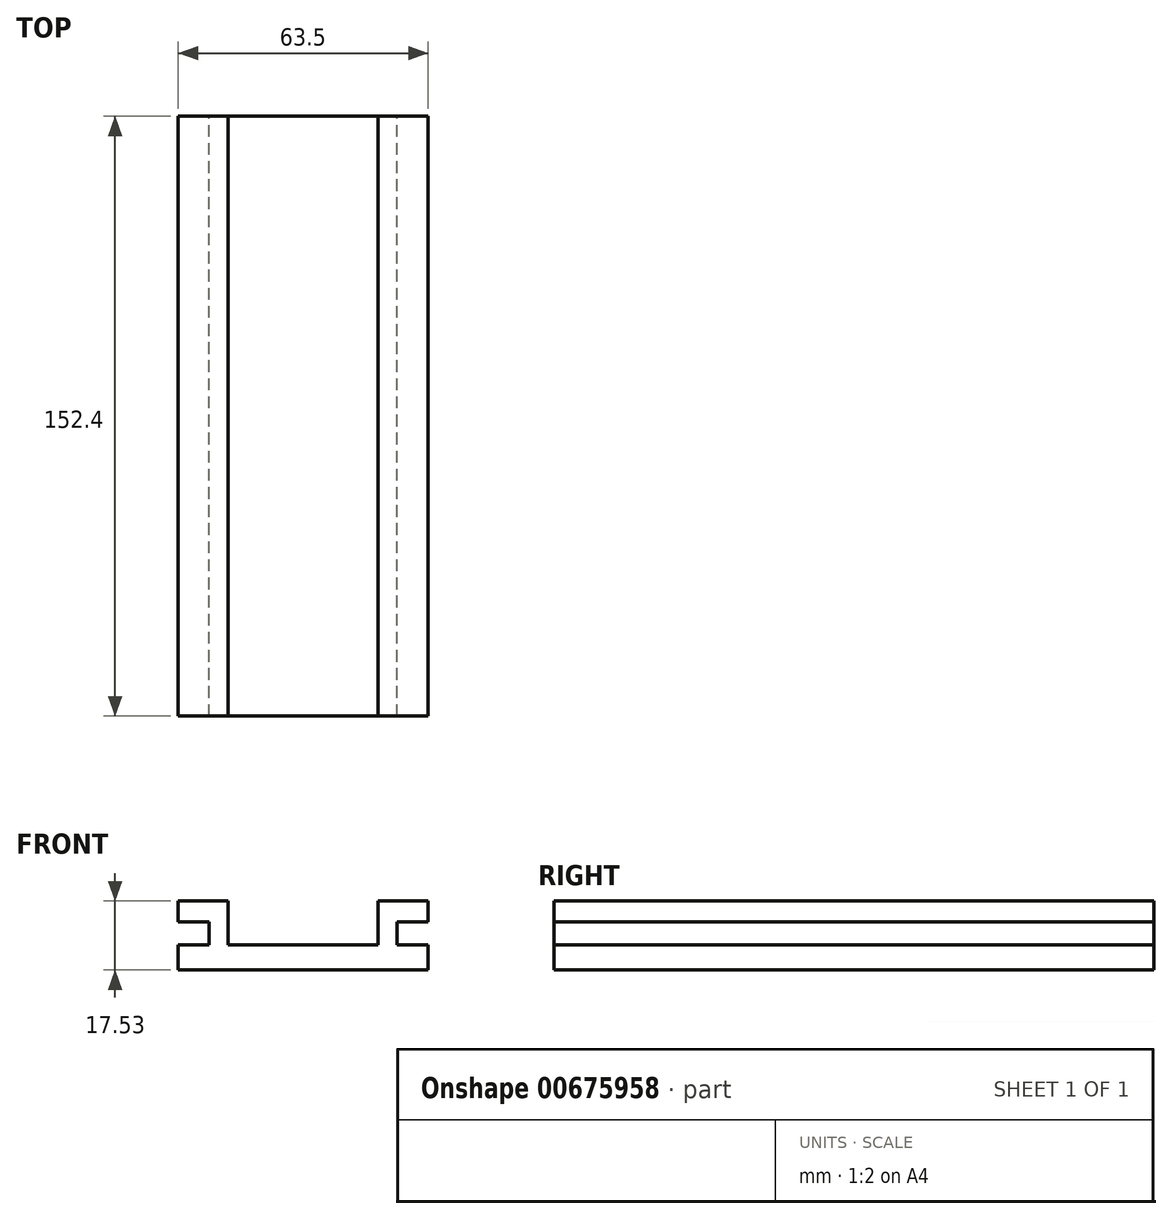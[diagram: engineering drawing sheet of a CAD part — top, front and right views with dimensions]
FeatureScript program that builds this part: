
annotation { "Feature Type Name" : "Feature", "Feature Type Description" : "" }
export const myFeature = defineFeature(function(context is Context, id is Id, definition is map)
    precondition{}
    {
        {
            var Q0;
            Q0=qCreatedBy(makeId("Front.planeOp"),FACE);
            var sketch = newSketch(context, id + "F0", { "sketchPlane" : qUnion([Q0])});
            skLineSegment(sketch, "E0", {"start": v(-31.75, 0) * mm, "end": v(-19.05, 0) * mm});
            skLineSegment(sketch, "E1", {"start": v(-31.75, 0) * mm, "end": v(-31.75, -5.33) * mm});
            skLineSegment(sketch, "E2", {"start": v(-31.75, -5.33) * mm, "end": v(-23.88, -5.33) * mm});
            skLineSegment(sketch, "E3", {"start": v(-23.88, -5.33) * mm, "end": v(-23.88, -11.18) * mm});
            skLineSegment(sketch, "E4", {"start": v(-23.88, -11.18) * mm, "end": v(-31.75, -11.18) * mm});
            skLineSegment(sketch, "E5", {"start": v(-31.75, -11.18) * mm, "end": v(-31.75, -17.53) * mm});
            skLineSegment(sketch, "E6", {"start": v(-19.05, 0) * mm, "end": v(-19.05, -11.18) * mm});
            skLineSegment(sketch, "E7", {"start": v(-31.75, -17.53) * mm, "end": v(0, -17.53) * mm});
            skLineSegment(sketch, "E8", {"start": v(-19.05, -11.18) * mm, "end": v(0, -11.18) * mm});
            skLineSegment(sketch, "E9.MirrorCS", {"start": v(31.75, -11.18) * mm, "end": v(31.75, -17.53) * mm});
            skLineSegment(sketch, "E10.MirrorCS", {"start": v(23.88, -5.33) * mm, "end": v(23.88, -11.18) * mm});
            skLineSegment(sketch, "E11.MirrorCS", {"start": v(31.75, 0) * mm, "end": v(31.75, -5.33) * mm});
            skLineSegment(sketch, "E12.MirrorCS", {"start": v(31.75, 0) * mm, "end": v(19.05, 0) * mm});
            skLineSegment(sketch, "E13.MirrorCS", {"start": v(31.75, -5.33) * mm, "end": v(23.88, -5.33) * mm});
            skLineSegment(sketch, "E14.MirrorCS", {"start": v(23.88, -11.18) * mm, "end": v(31.75, -11.18) * mm});
            skLineSegment(sketch, "E15.MirrorCS", {"start": v(19.05, -11.18) * mm, "end": v(0, -11.18) * mm});
            skLineSegment(sketch, "E16.MirrorCS", {"start": v(31.75, -17.53) * mm, "end": v(0, -17.53) * mm});
            skLineSegment(sketch, "E17.MirrorCS", {"start": v(19.05, 0) * mm, "end": v(19.05, -11.18) * mm});
            skSolve(sketch);
        }
        {
            var Q0;
            Q0 = qSketchRegion(id + "F0", true);
            extrude(context, id + "F1", {"entities" : qUnion([Q0]), "endBound" : BoundingType.SYMMETRIC, "depth" : 152.4 * mm, "offsetDistance" : 25.4 * mm});
        }
    });
